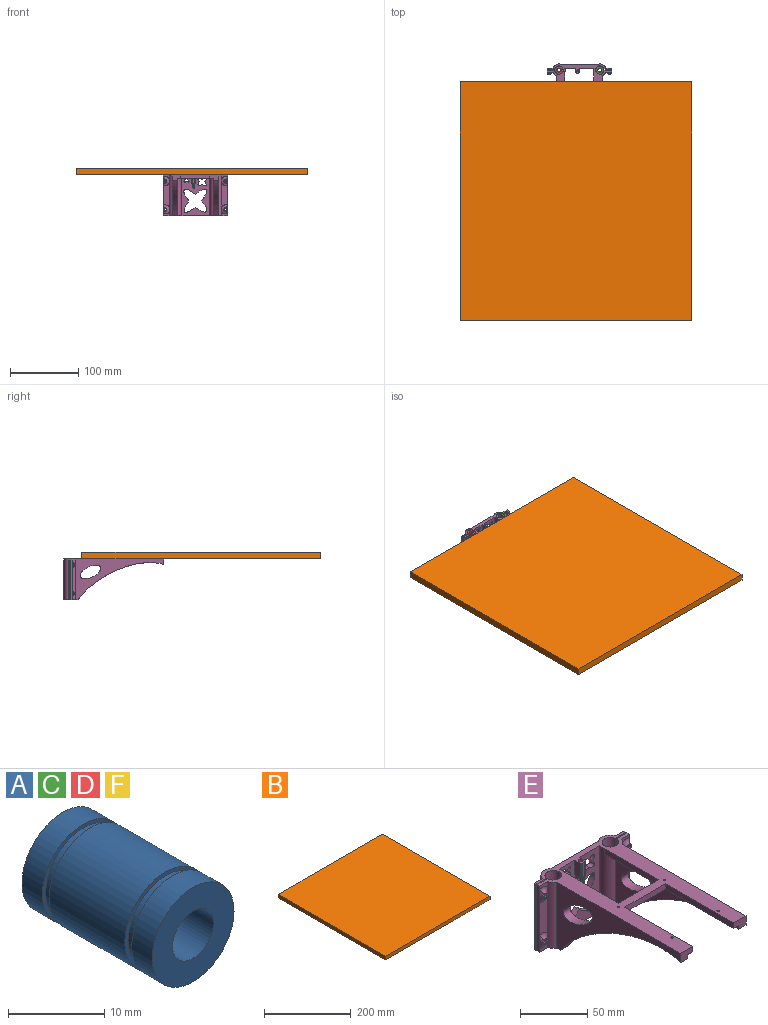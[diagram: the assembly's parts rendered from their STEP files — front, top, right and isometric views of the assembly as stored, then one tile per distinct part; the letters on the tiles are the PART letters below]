
ASSEMBLY  parts=6 mates=5
PART A: 12 faces, bbox 12x19.1x12 mm
  f0: cylinder r=3mm len=19.1mm, axis (0,1,0), area 360mm2, adj f3,f10
  f1: cylinder r=6mm len=12mm, axis (0,1,0), area 113.1mm2, adj f2,f3
  f2: plane 12x12mm, normal (0,-1,0), area 18.1mm2, adj f1,f4
  f3: plane 12x12mm, normal (0,1,0), area 84.8mm2, adj f0,f1
  f4: cylinder r=5.5mm len=11mm, axis (0,1,0), area 34.6mm2, adj f2,f7
  f5: cylinder r=6mm len=12mm, axis (0,1,0), area 418.5mm2, adj f6,f7
  f6: plane 12x12mm, normal (0,-1,0), area 18.1mm2, adj f5,f8
  f7: plane 12x12mm, normal (0,1,0), area 18.1mm2, adj f4,f5
  f8: cylinder r=5.5mm len=11mm, axis (0,1,0), area 34.6mm2, adj f6,f11
  f9: cylinder r=6mm len=12mm, axis (0,1,0), area 113.1mm2, adj f10,f11
  f10: plane 12x12mm, normal (0,-1,0), area 84.8mm2, adj f0,f9
  f11: plane 12x12mm, normal (0,1,0), area 18.1mm2, adj f8,f9
PART B: 6 faces, bbox 340x350x10 mm
  f0: plane 340x10mm, normal (0,1,0), area 3400mm2, adj f1,f3,f4,f5
  f1: plane 350x10mm, normal (-1,0,0), area 3500mm2, adj f0,f2,f4,f5
  f2: plane 340x10mm, normal (0,-1,0), area 3400mm2, adj f1,f3,f4,f5
  f3: plane 350x10mm, normal (1,0,0), area 3500mm2, adj f0,f2,f4,f5
  f4: plane 350x340mm, normal (0,0,1), area 119000mm2, adj f0,f1,f2,f3
  f5: plane 350x340mm, normal (0,0,-1), area 119000mm2, adj f0,f1,f2,f3
PART C: same geometry as A
PART D: same geometry as A
PART E: 113 faces, bbox 98.3x147.2x63.8 mm
  f0: plane 60x42.49mm, normal (0,-1,0), area 1518.8mm2, adj f5,f6,f8,f42,f69,f70,f71,f72
  f1: plane 34.73x8.59mm, normal (0,-1,0), area 255.9mm2, adj f12,f14,f33,f35
  f2: plane 8.59x5.4mm, normal (0,-1,0), area 25.2mm2, adj f5,f12,f14,f35
  f3: plane 60x1.99mm, normal (-1,0,0), area 119.7mm2, adj f5,f6,f11,f26
  f4: cylinder r=6.1mm len=60mm, axis (0,0,-1), area 2239.4mm2, adj f5,f6,f25,f26
  f5: plane 147.12x94.42mm, normal (0,0,1), area 4277.6mm2, adj f0,f2,f3,f4,f8,f9,f10,f11
  f6: plane 94.42x20.96mm, normal (0,0,-1), area 631.8mm2, adj f0,f3,f4,f7,f8,f9,f10,f11
  f7: plane 129.51x55mm, normal (1,0,0), area 1650.5mm2, adj f6,f8,f16,f17,f18,f68
  f8: cylinder r=9.1mm len=60mm, axis (0,0,-1), area 769.7mm2, adj f0,f5,f6,f7,f18,f20
  f9: plane 60x49.62mm, normal (0,1,0), area 2032.6mm2, adj f5,f6,f10,f43,f77,f78,f79,f80
  f10: cylinder r=9.1mm len=60mm, axis (0,0,-1), area 1010.3mm2, adj f5,f6,f9,f11
  f11: plane 60x8.59mm, normal (0,1,0), area 502.4mm2, adj f3,f5,f6,f10,f27,f29
  f12: plane 60x2.83mm, normal (-1,0,0), area 170mm2, adj f1,f2,f5,f6,f13,f25,f34,f36
  f13: plane 8.59x5.91mm, normal (0,-1,0), area 29.6mm2, adj f6,f12,f14,f33
  f14: cylinder r=9.1mm len=60mm, axis (0,0,-1), area 411.3mm2, adj f1,f2,f5,f6,f13,f15,f33,f35
  f15: plane 130x60mm, normal (-1,0,0), area 2327.6mm2, adj f5,f6,f14,f16,f17,f68
  f16: plane 12.96x8.39mm, normal (0,-1,0), area 90.2mm2, adj f5,f7,f15,f17,f18,f21
  f17: extruded ~126.16x54.74mm, area 1078.3mm2, adj f6,f7,f15,f16
  f18: plane 135.26x53.58mm, normal (0,0,-1), area 1725.6mm2, adj f7,f8,f16,f19,f20,f21,f22,f23
  f19: plane 42.67x5mm, normal (0,1,0), area 213.3mm2, adj f5,f18,f20,f51
  f20: plane 56.76x5mm, normal (1,0,0), area 283.8mm2, adj f5,f8,f18,f19
  f21: plane 71.5x5mm, normal (1,0,0), area 357.5mm2, adj f5,f16,f18,f22
  f22: plane 42.67x5mm, normal (0,-1,0), area 213.3mm2, adj f5,f18,f21,f52
  f23: cylinder r=0.84mm len=5mm, axis (0,0,1), area 26.3mm2, adj f5,f18
  f24: cylinder r=0.84mm len=5mm, axis (0,0,1), area 26.3mm2, adj f5,f18
  f25: plane 60x11.11mm, normal (0,1,0), area 653.3mm2, adj f4,f5,f6,f12,f28,f30
  f26: plane 60x11.18mm, normal (0,-1,0), area 657.5mm2, adj f3,f4,f5,f6,f27,f29
  f27: cylinder r=1.45mm len=2.9mm, axis (0,-1,0), area 18.2mm2, adj f11,f26
  f28: cylinder r=1.45mm len=5.83mm, axis (0,-1,0), area 53.1mm2, adj f25,f32
  f29: cylinder r=1.45mm len=2.9mm, axis (0,-1,0), area 18.2mm2, adj f11,f26
  f30: cylinder r=1.45mm len=5.83mm, axis (0,-1,0), area 53.1mm2, adj f25,f31
  f31: torus R=1.45mm, axis (0,-1,0), area 13.9mm2, adj f30,f35,f36
  f32: torus R=1.45mm, axis (0,-1,0), area 13.9mm2, adj f28,f33,f34
  f33: torus R=6.65mm, axis (0,1,0), area 85.9mm2, adj f1,f13,f14,f32,f34
  f34: bspline ~12.5x2.69mm, area 20.8mm2, adj f12,f32,f33
  f35: torus R=6.65mm, axis (0,1,0), area 85.9mm2, adj f1,f2,f14,f31,f36
  f36: bspline ~12.5x2.69mm, area 20.8mm2, adj f12,f31,f35
  f37: plane 34.73x8.59mm, normal (0,-1,0), area 255.9mm2, adj f45,f47,f63,f65
  f38: plane 8.59x5.4mm, normal (0,-1,0), area 25.2mm2, adj f5,f45,f47,f65
  f39: plane 60x1.99mm, normal (1,0,0), area 119.7mm2, adj f5,f6,f44,f56
  f40: cylinder r=6.1mm len=60mm, axis (0,0,-1), area 2239.4mm2, adj f5,f6,f55,f56
  f41: plane 129.51x55mm, normal (-1,0,0), area 1650.5mm2, adj f6,f18,f42,f49,f50,f67
  f42: cylinder r=9.1mm len=60mm, axis (0,0,-1), area 769.7mm2, adj f0,f5,f6,f18,f41,f51
  f43: cylinder r=9.1mm len=60mm, axis (0,0,-1), area 1010.3mm2, adj f5,f6,f9,f44
  f44: plane 60x8.59mm, normal (0,1,0), area 502.4mm2, adj f5,f6,f39,f43,f57,f59
  f45: plane 60x2.83mm, normal (1,0,0), area 170mm2, adj f5,f6,f37,f38,f46,f55,f64,f66
  f46: plane 8.59x5.91mm, normal (0,-1,0), area 29.6mm2, adj f6,f45,f47,f63
  f47: cylinder r=9.1mm len=60mm, axis (0,0,-1), area 411.3mm2, adj f5,f6,f37,f38,f46,f48,f63,f65
  f48: plane 130x60mm, normal (1,0,0), area 2327.6mm2, adj f5,f6,f47,f49,f50,f67
  f49: plane 12.96x8.39mm, normal (0,-1,0), area 90.2mm2, adj f5,f18,f41,f48,f50,f52
  f50: extruded ~126.16x54.74mm, area 1078.3mm2, adj f6,f41,f48,f49
  f51: plane 56.76x5mm, normal (-1,0,0), area 283.8mm2, adj f5,f18,f19,f42
  f52: plane 71.5x5mm, normal (-1,0,0), area 357.5mm2, adj f5,f18,f22,f49
  f53: cylinder r=0.84mm len=5mm, axis (0,0,1), area 26.3mm2, adj f5,f18
  f54: cylinder r=0.84mm len=5mm, axis (0,0,1), area 26.3mm2, adj f5,f18
  f55: plane 60x11.11mm, normal (0,1,0), area 653.3mm2, adj f5,f6,f40,f45,f58,f60
  f56: plane 60x11.18mm, normal (0,-1,0), area 657.5mm2, adj f5,f6,f39,f40,f57,f59
  f57: cylinder r=1.45mm len=2.9mm, axis (0,-1,0), area 18.2mm2, adj f44,f56
  f58: cylinder r=1.45mm len=5.83mm, axis (0,-1,0), area 53.1mm2, adj f55,f62
  f59: cylinder r=1.45mm len=2.9mm, axis (0,-1,0), area 18.2mm2, adj f44,f56
  f60: cylinder r=1.45mm len=5.83mm, axis (0,-1,0), area 53.1mm2, adj f55,f61
  f61: torus R=1.45mm, axis (0,-1,0), area 13.9mm2, adj f60,f65,f66
  f62: torus R=1.45mm, axis (0,-1,0), area 13.9mm2, adj f58,f63,f64
  f63: torus R=6.65mm, axis (0,1,0), area 85.9mm2, adj f37,f46,f47,f62,f64
  f64: bspline ~12.5x2.69mm, area 20.8mm2, adj f45,f62,f63
  f65: torus R=6.65mm, axis (0,1,0), area 85.9mm2, adj f37,f38,f47,f61,f66
  f66: bspline ~12.5x2.69mm, area 20.8mm2, adj f45,f61,f65
  f67: extruded ~30.64x20.11mm, area 594.3mm2, adj f41,f48
  f68: extruded ~30.64x20.11mm, area 594.3mm2, adj f7,f15
  f69: plane 6x5mm, normal (-1,0,0), area 25.1mm2, adj f0,f89,f98,f100,f102
  f70: plane 6x0.17mm, normal (0,0,-1), area 1mm2, adj f0,f97,f107,f110
  f71: plane 6x5mm, normal (1,0,0), area 25.1mm2, adj f0,f89,f91,f94,f95
  f72: plane 13x6mm, normal (1,0,0), area 78mm2, adj f0,f5,f90,f91
  f73: plane 13x6mm, normal (-1,0,0), area 78mm2, adj f0,f5,f102,f104
  f74: plane 19x2.17mm, normal (0,-1,0), area 29.3mm2, adj f5,f93,f97,f101,f105,f108,f111,f112
  f75: cylinder r=1.4mm len=15mm, axis (0,0,1), area 131.9mm2, adj f5,f76
  f76: plane 2.8x2.8mm, normal (0,0,1), area 6.2mm2, adj f75
  f77: extruded ~6.02x5.39mm, area 58.2mm2, adj f0,f9,f78,f80
  f78: extruded ~6.02x5.39mm, area 58.2mm2, adj f0,f9,f77,f79
  f79: extruded ~6.02x5.39mm, area 58.2mm2, adj f0,f9,f78,f80
  f80: extruded ~6.02x5.39mm, area 58.2mm2, adj f0,f9,f77,f79
  f81: extruded ~5x3.7mm, area 40.4mm2, adj f0,f9,f82,f84
  f82: extruded ~5x3.71mm, area 40.4mm2, adj f0,f9,f81,f83
  f83: extruded ~5x3.7mm, area 40.4mm2, adj f0,f9,f82,f84
  f84: extruded ~5x3.71mm, area 40.4mm2, adj f0,f9,f81,f83
  f85: extruded ~16.68x16.64mm, area 181mm2, adj f0,f9,f86,f88
  f86: extruded ~16.76x16.55mm, area 181mm2, adj f0,f9,f85,f87
  f87: extruded ~16.68x16.64mm, area 181mm2, adj f0,f9,f86,f88
  f88: extruded ~16.76x16.55mm, area 181mm2, adj f0,f9,f85,f87
  f89: cylinder r=1.25mm len=3mm, axis (1,0,0), area 23.6mm2, adj f69,f71
  f90: plane 13x0.71mm, normal (0.71,-0.71,0), area 13mm2, adj f5,f72,f92,f112
  f91: plane 6x1mm, normal (0.71,0,-0.71), area 8.5mm2, adj f0,f71,f72,f92
  f92: plane 1.04x1.04mm, normal (0.58,-0.58,-0.58), area 0.8mm2, adj f90,f91,f93,f112
  f93: plane 1.46x1.04mm, normal (0,-0.71,-0.71), area 0.7mm2, adj f74,f92,f94,f105,f112
  f94: plane 5.71x0.71mm, normal (0.71,-0.71,0), area 5.4mm2, adj f71,f93,f96,f105
  f95: plane 6x0.71mm, normal (0.71,0,-0.71), area 6mm2, adj f0,f71,f96,f107
  f96: plane 0.74x0.74mm, normal (0.58,-0.58,-0.58), area 0.5mm2, adj f94,f95,f105,f106,f107
  f97: plane 1x1mm, normal (0,-0.71,-0.71), area 0.5mm2, adj f70,f74,f105,f106,f107,f108,f109,f110
  f98: plane 6x0.71mm, normal (-0.71,0,-0.71), area 6mm2, adj f0,f69,f99,f110
  f99: plane 0.74x0.74mm, normal (-0.58,-0.58,-0.58), area 0.5mm2, adj f98,f100,f108,f109,f110
  f100: plane 5.71x0.71mm, normal (-0.71,-0.71,0), area 5.4mm2, adj f69,f99,f101,f108
  f101: plane 1.46x1.04mm, normal (0,-0.71,-0.71), area 0.7mm2, adj f74,f100,f103,f108,f111
  f102: plane 6x1mm, normal (-0.71,0,-0.71), area 8.5mm2, adj f0,f69,f73,f103
  f103: plane 1.04x1.04mm, normal (-0.58,-0.58,-0.58), area 0.8mm2, adj f101,f102,f104,f111
  f104: plane 13x0.71mm, normal (-0.71,-0.71,0), area 13mm2, adj f5,f73,f103,f111
  f105: cylinder r=1mm len=6mm, axis (0,0,1), area 4.6mm2, adj f74,f93,f94,f96,f97,f106
  f106: cylinder r=1mm len=1.12mm, axis (0,-0.71,0.71), area 0.8mm2, adj f96,f97,f105,f107
  f107: cylinder r=1mm len=6mm, axis (0,-1,0), area 4.7mm2, adj f0,f70,f95,f96,f97,f106
  f108: cylinder r=1mm len=6mm, axis (0,0,1), area 4.6mm2, adj f74,f97,f99,f100,f101,f109
  f109: cylinder r=1mm len=1.12mm, axis (0,-0.71,0.71), area 0.8mm2, adj f97,f99,f108,f110
  f110: cylinder r=1mm len=6mm, axis (0,-1,0), area 4.7mm2, adj f0,f70,f97,f98,f99,f109
  f111: cylinder r=1mm len=13.09mm, axis (0,0,1), area 10.2mm2, adj f5,f74,f101,f103,f104
  f112: cylinder r=1mm len=13.09mm, axis (0,0,1), area 10.2mm2, adj f5,f74,f90,f92,f93
PART F: same geometry as A
PLACE A rot(axis=(1,0,0),90deg) t=(-37.94,47.01,30.64)mm
PLACE B t=(-198.06,-178.7,71.54)mm
PLACE C rot(axis=(1,0,0),90deg) t=(-37.94,47.01,71.54)mm
PLACE D rot(axis=(-1,0,0),90deg) t=(-97.94,47.01,52.44)mm
PLACE E t=(-69.66,49.49,11.54)mm
PLACE F rot(axis=(1,0,0),90deg) t=(-97.94,47.01,30.64)mm
MATE fastened D.f0 <-> E.f4  axis (0,0,1) through (-97.94,47.01,71.54)mm
MATE fastened C.f0 <-> E.f40  axis (0,0,1) through (-37.94,47.01,71.54)mm
MATE fastened F.f0 <-> E.f4  axis (0,0,-1) through (-97.94,47.01,11.54)mm
MATE fastened B.f5 <-> E.f5  axis (0,0,-1) through (-72.94,29.49,71.54)mm
MATE fastened A.f0 <-> E.f40  axis (0,0,-1) through (-37.94,47.01,11.54)mm
